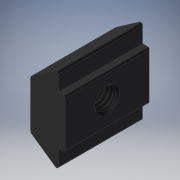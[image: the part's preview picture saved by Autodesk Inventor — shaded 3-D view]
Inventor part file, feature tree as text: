
AUTODESK INVENTOR PART (.ipt)
format: ipt  version: 2019 (Build 230136000, 136)  size: 145,920 bytes
history: native  units: mm
features: other x28, sketch x2, extrude x1, revolve x1, thread x1
ambient origin geometry x8: Origin, YZ Plane, XZ Plane, XY Plane, X Axis, Y Axis, Z Axis, Center Point
bodies: Solid1 (feature_tree)
feature tree (33):
  extrude  "Extrusion1"  TaperAngle=360.0deg  [1 undecoded]
  revolve  "Revolution1"  [1 undecoded]
  thread  "Thread1"  [1 undecoded]
  other  "nut_XY"
  other  "nut_YZ"
  other  "nut_ZX"
  other  "nut_X"
  other  "nut_Y"
  other  "nut_Z"
  other  "nut_Center"
  other  "to_bolt_XY"
  other  "to_bolt_YZ"
  other  "to_bolt_ZX"
  other  "to_bolt_X"
  other  "to_bolt_Y"
  other  "to_bolt_Z"
  other  "to_bolt_Center"
  other  "to_frames_XY"
  other  "to_frames_YZ"
  other  "to_frames_ZX"
  other  "to_frames_X"
  other  "to_frames_Y"
  other  "to_frames_Z"
  other  "to_frames_Center"
  other  "to_lane_XY"
  other  "to_lane_YZ"
  other  "to_lane_ZX"
  other  "to_lane_X"
  other  "to_lane_Y"
  other  "to_lane_Z"
  other  "to_lane_Center"
  sketch  "Sketch_2"  dims[d0=10.0mm d1=0.0mm d2=360.0deg]
  sketch  "Sketch_5"  dims[d3=3.559mm d4=0.0mm d5=0.0mm d6=0.0mm]
note: 3 required parameter values undecoded (feature->parameter linkage not recoverable at this tier; creation-order binding heuristic only, values carry confidence <= 0.55)